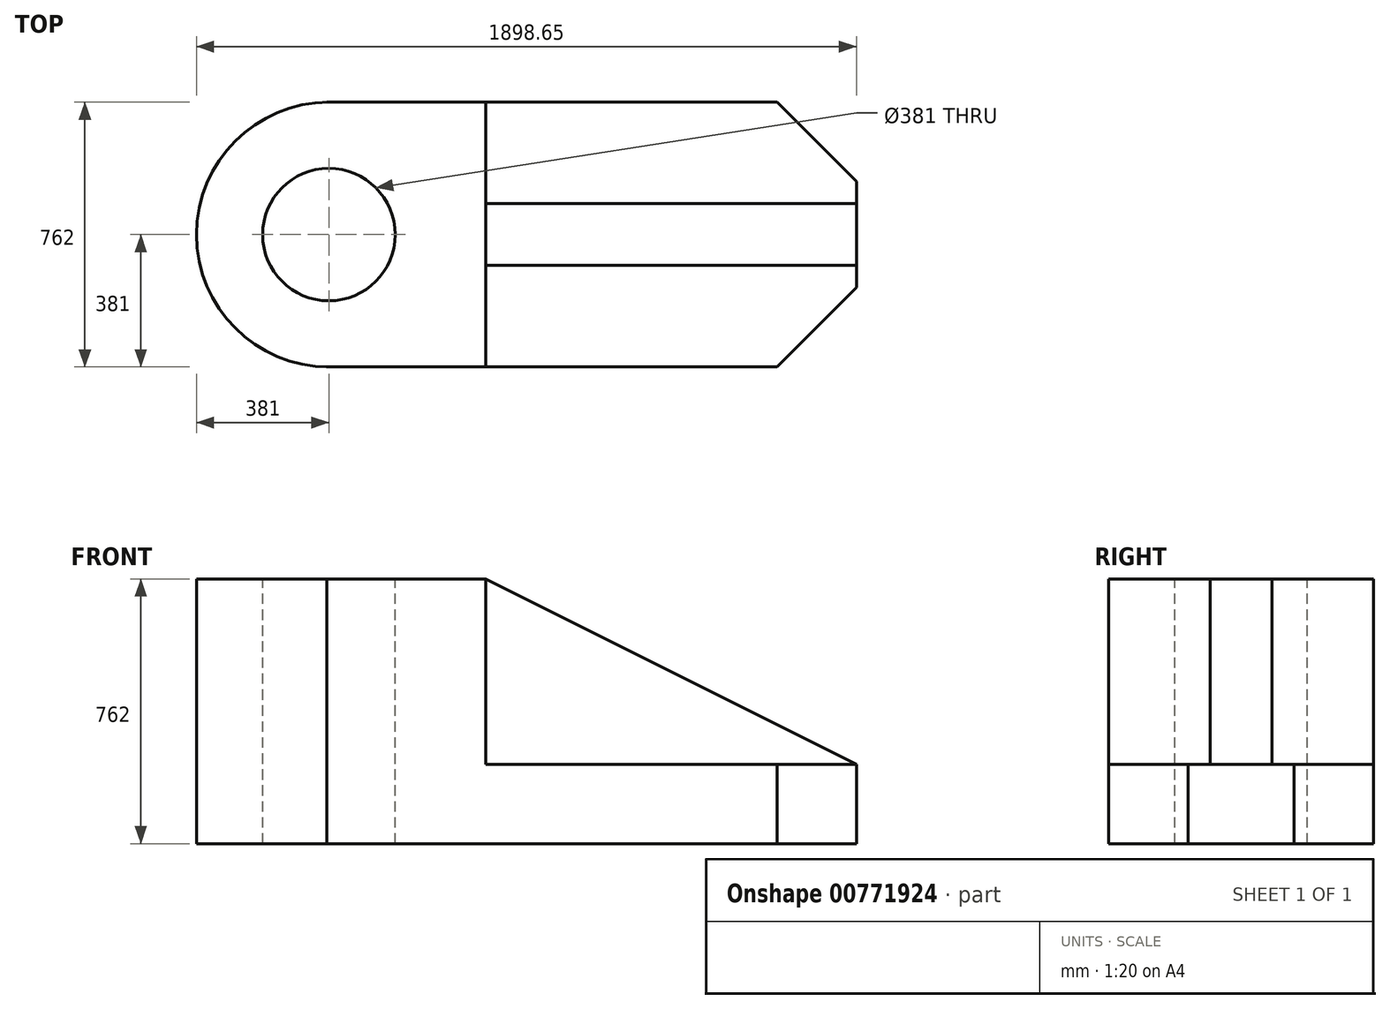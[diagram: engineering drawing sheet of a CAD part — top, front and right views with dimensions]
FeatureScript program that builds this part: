
annotation { "Feature Type Name" : "Feature", "Feature Type Description" : "" }
export const myFeature = defineFeature(function(context is Context, id is Id, definition is map)
    precondition{}
    {
        {
            var Q0;
            Q0=qCreatedBy(makeId("Front.planeOp"),FACE);
            var sketch = newSketch(context, id + "F0", { "sketchPlane" : qUnion([Q0])});
            skLineSegment(sketch, "E0", {"start": v(6.35, 0) * mm, "end": v(1524, 0) * mm});
            skLineSegment(sketch, "E1", {"start": v(1524, 0) * mm, "end": v(1524, 762) * mm});
            skPoint(sketch, "E2.visualSharp", {"position": v(0, 762) * mm});
            skLineSegment(sketch, "E3", {"start": v(6.35, 762) * mm, "end": v(1524, 762) * mm});
            skLineSegment(sketch, "E4", {"start": v(0, 6.35) * mm, "end": v(0, 755.65) * mm});
            skArc(sketch, "E5.filletArc", {"start": v(6.35, 762) * mm, "mid": v(1.86, 760.14) * mm, "end": v(0, 755.65) * mm});
            skPoint(sketch, "E6.visualSharp", {"position": v(0, 0) * mm});
            skArc(sketch, "E6.filletArc", {"start": v(0, 6.35) * mm, "mid": v(1.86, 1.86) * mm, "end": v(6.35, 0) * mm});
            skSolve(sketch);
        }
        {
            var Q0;
            Q0 = qSketchRegion(id + "F0", true);
            extrude(context, id + "F1", {"entities" : qUnion([Q0]), "depth" : 762 * mm, "offsetDistance" : 25.4 * mm});
        }
        {
            var Q0;
            Q0=makeQuery(id+"F1.opExtrude","SWEPT_FACE",FACE,{"disambiguationData":[OSD([sQuery(id+"F0.wireOp",EDGE,"E3")])]});
            var sketch = newSketch(context, id + "F2", { "sketchPlane" : qUnion([Q0])});
            skLineSegment(sketch, "E7", {"start": v(1524, 0) * mm, "end": v(1524, -228.6) * mm});
            skLineSegment(sketch, "E8", {"start": v(1524, 0) * mm, "end": v(1295.4, 0) * mm});
            skLineSegment(sketch, "E9", {"start": v(1295.4, 0) * mm, "end": v(1524, -228.6) * mm});
            skLineSegment(sketch, "E10", {"start": v(1524, -762) * mm, "end": v(1524, -533.4) * mm});
            skLineSegment(sketch, "E11", {"start": v(1524, -762) * mm, "end": v(1295.4, -762) * mm});
            skLineSegment(sketch, "E12", {"start": v(1295.4, -762) * mm, "end": v(1524, -533.4) * mm});
            skLineSegment(sketch, "E13", {"start": v(457.2, 0) * mm, "end": v(457.2, -292.1) * mm});
            skLineSegment(sketch, "E14", {"start": v(457.2, -762) * mm, "end": v(457.2, -469.9) * mm});
            skLineSegment(sketch, "E15", {"start": v(457.2, -469.9) * mm, "end": v(1524, -469.9) * mm});
            skLineSegment(sketch, "E16", {"start": v(1524, -469.9) * mm, "end": v(1524, -533.4) * mm});
            skLineSegment(sketch, "E17", {"start": v(457.2, -292.1) * mm, "end": v(1524, -292.1) * mm});
            skLineSegment(sketch, "E18", {"start": v(1524, -292.1) * mm, "end": v(1524, -228.6) * mm});
            skSolve(sketch);
        }
        {
            var Q0;
            Q0=makeQuery(id+"F2.imprint","IMPRINT",FACE,{"disambiguationData":[TD([[makeQuery(id+"F2.imprint","IMPRINT",EDGE,{"derivedFrom":sQuery(id+"F2.wireOp",EDGE,"E7")}),1.0]])]});
            var Q1;
            Q1=makeQuery(id+"F2.imprint","IMPRINT",FACE,{"disambiguationData":[TD([[makeQuery(id+"F2.imprint","IMPRINT",EDGE,{"derivedFrom":sQuery(id+"F2.wireOp",EDGE,"E10")}),1.0]])]});
            extrude(context, id + "F3", {"entities" : qUnion([Q0, Q1]), "operationType" : NewBodyOperationType.REMOVE, "endBound" : BoundingType.THROUGH_ALL, "oppositeDirection" : true, "depth" : 25.4 * mm, "offsetDistance" : 25.4 * mm});
        }
        {
            var Q0;
            {var subQ1=sQuery(id+"F2.wireOp",EDGE,"E9");Q0=makeQuery(id+"F2.imprint","IMPRINT",FACE,{"disambiguationData":[TD([[makeQuery(id+"F2.imprint","IMPRINT",EDGE,{"derivedFrom":subQ1}),-1.0]])]});}
            var Q1;
            {var subQ1=sQuery(id+"F2.wireOp",EDGE,"E12");Q1=makeQuery(id+"F2.imprint","IMPRINT",FACE,{"disambiguationData":[TD([[makeQuery(id+"F2.imprint","IMPRINT",EDGE,{"derivedFrom":subQ1}),1.0]])]});}
            extrude(context, id + "F4", {"entities" : qUnion([Q0, Q1]), "operationType" : NewBodyOperationType.REMOVE, "oppositeDirection" : true, "depth" : 533.4 * mm, "offsetDistance" : 25.4 * mm});
        }
        {
            var Q0;
            Q0=makeQuery(id+"F4.boolean.opBoolean","COPY",FACE,{"derivedFrom":makeQuery(id+"F4.opExtrude","SWEPT_FACE",FACE,{"disambiguationData":[OSD([sQuery(id+"F2.wireOp",EDGE,"E15")])]})});
            var sketch = newSketch(context, id + "F5", { "sketchPlane" : qUnion([Q0])});
            skLineSegment(sketch, "E19", {"start": v(457.2, 762) * mm, "end": v(1524, 228.6) * mm});
            skSolve(sketch);
        }
        {
            var Q0;
            Q0=makeQuery(id+"F5.imprint","IMPRINT",FACE,{"disambiguationData":[TD([[makeQuery(id+"F5.imprint","IMPRINT",EDGE,{"derivedFrom":sQuery(id+"F5.wireOp",EDGE,"E19")}),1.0]])]});
            extrude(context, id + "F6", {"entities" : qUnion([Q0]), "operationType" : NewBodyOperationType.REMOVE, "endBound" : BoundingType.THROUGH_ALL, "oppositeDirection" : true, "depth" : 25.4 * mm, "offsetDistance" : 25.4 * mm});
        }
        {
            var Q0;
            Q0=makeQuery(id+"F1.opExtrude","SWEPT_FACE",FACE,{"disambiguationData":[OSD([sQuery(id+"F0.wireOp",EDGE,"E3")])]});
            var sketch = newSketch(context, id + "F7", { "sketchPlane" : qUnion([Q0])});
            skArc(sketch, "E20", {"start": v(6.35, 0) * mm, "mid": v(-374.65, -381) * mm, "end": v(6.35, -762) * mm});
            skCircle(sketch, "E21", {"center": v(6.35, -381) * mm, "radius": 190.5 * mm});
            skSolve(sketch);
        }
        {
            var Q0;
            {var subQ0=sQuery(id+"F7.wireOp",EDGE,"E20");Q0=makeQuery(id+"F7.imprint","IMPRINT",FACE,{"disambiguationData":[TD([[makeQuery(id+"F7.imprint","IMPRINT",EDGE,{"derivedFrom":subQ0}),1.0]])]});}
            extrude(context, id + "F8", {"entities" : qUnion([Q0]), "operationType" : NewBodyOperationType.ADD, "oppositeDirection" : true, "depth" : 762 * mm, "offsetDistance" : 25.4 * mm});
        }
        {
            var Q0;
            Q0 = qSketchRegion(id + "F7", true);
            extrude(context, id + "F9", {"entities" : qUnion([Q0]), "operationType" : NewBodyOperationType.REMOVE, "endBound" : BoundingType.THROUGH_ALL, "oppositeDirection" : true, "depth" : 25.4 * mm, "offsetDistance" : 25.4 * mm});
        }
    });
